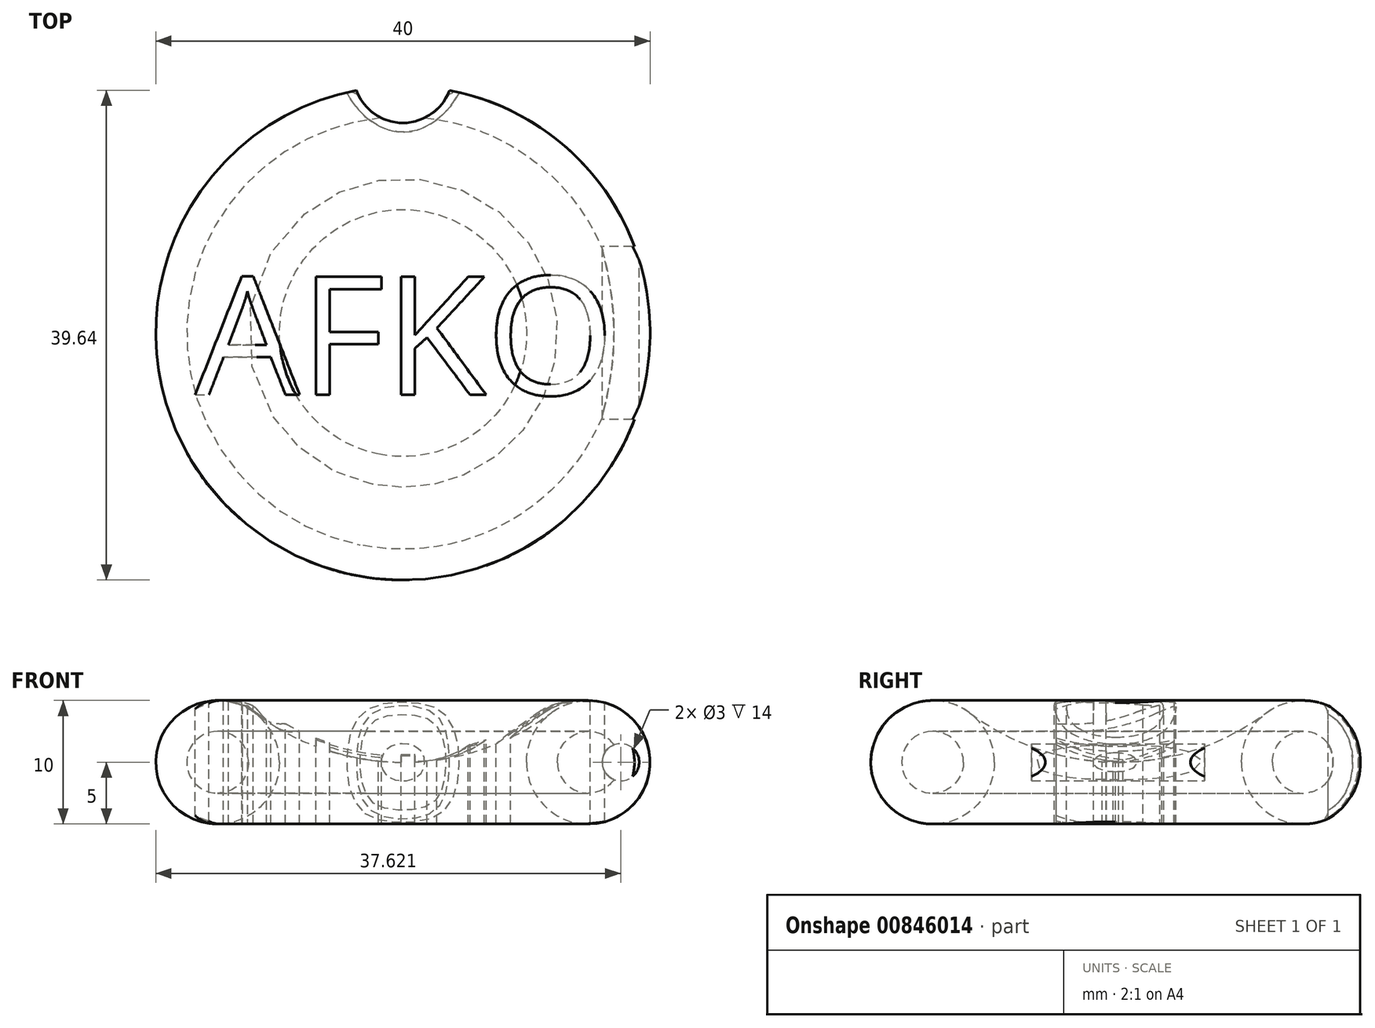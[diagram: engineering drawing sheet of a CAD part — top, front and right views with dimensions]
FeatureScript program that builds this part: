
annotation { "Feature Type Name" : "Feature", "Feature Type Description" : "" }
export const myFeature = defineFeature(function(context is Context, id is Id, definition is map)
    precondition{}
    {
        {
            var Q0;
            Q0=qCreatedBy(makeId("Front.planeOp"),FACE);
            var sketch = newSketch(context, id + "F0", { "sketchPlane" : qUnion([Q0])});
            skArc(sketch, "E0", {"start": v(-12, 9) * mm, "mid": v(-6.32, 6.03) * mm, "end": v(0, 5) * mm});
            skArc(sketch, "E1", {"start": v(-12, 9) * mm, "mid": v(-19.74, 6.58) * mm, "end": v(-15, 0) * mm});
            skLineSegment(sketch, "E2", {"start": v(-15, 0) * mm, "end": v(0, 0) * mm});
            skLineSegment(sketch, "E3", {"start": v(0, 0) * mm, "end": v(0, 5) * mm});
            skSolve(sketch);
        }
        {
            var Q0;
            Q0=makeQuery(id+"F0.imprint","IMPRINT",FACE,{"disambiguationData":[TD([[makeQuery(id+"F0.imprint","IMPRINT",EDGE,{"derivedFrom":sQuery(id+"F0.wireOp",EDGE,"E0")}),-1.0]])]});
            var Q1;
            Q1=sQuery(id+"F0.wireOp",EDGE,"E3");
            revolve(context, id + "F1", {"surfaceOperationType" : NewSurfaceOperationType.NEW, "entities" : qUnion([Q0]), "axis" : qUnion([Q1]), "revolveType" : RevolveType.FULL});
        }
        {
            var Q0;
            Q0=qCreatedBy(makeId("Top.planeOp"),FACE);
            cPlane(context, id + "F2", {"entities" : qUnion([Q0]), "cplaneType" : CPlaneType.OFFSET, "offset" : 25 * mm, "width" : 150 * mm, "height" : 150 * mm});
        }
        {
            var Q0;
            Q0=qCreatedBy(id+"F2.planeOp",FACE);
            var sketch = newSketch(context, id + "F3", { "sketchPlane" : qUnion([Q0])});
            skText(sketch, "E4", { "text": "AFKO", "fontName": "OpenSans-Regular.ttf"});
            const initialGuessF3  = {"E4": [-0.01682, -0.005, 1, 0, 0.00962]};
            skSetInitialGuess(sketch, initialGuessF3);
            skSolve(sketch);
        }
        {
            var Q0;
            Q0 = qSketchRegion(id + "F3", true);
            extrude(context, id + "F4", {"entities" : qUnion([Q0]), "operationType" : NewBodyOperationType.REMOVE, "oppositeDirection" : true, "depth" : 25 * mm, "offsetDistance" : 25 * mm});
        }
        {
            var Q0;
            Q0=qCreatedBy(makeId("Front.planeOp"),FACE);
            var sketch = newSketch(context, id + "F5", { "sketchPlane" : qUnion([Q0])});
            skCircle(sketch, "E5", {"center": v(-15, 5) * mm, "radius": 2.5 * mm});
            skCircle(sketch, "E6", {"center": v(-15, 5) * mm, "radius": 5 * mm});
            skSolve(sketch);
        }
        {
            var Q0;
            Q0 = qSketchRegion(id + "F5", true);
            var Q1;
            Q1=sQuery(id+"F0.wireOp",EDGE,"E3");
            revolve(context, id + "F6", {"surfaceOperationType" : NewSurfaceOperationType.NEW, "entities" : qUnion([Q0]), "axis" : qUnion([Q1]), "revolveType" : RevolveType.FULL});
        }
        {
            var Q0;
            Q0=qCreatedBy(id+"F2.planeOp",FACE);
            var sketch = newSketch(context, id + "F7", { "sketchPlane" : qUnion([Q0])});
            skCircle(sketch, "E7", {"center": v(0, 21) * mm, "radius": 4 * mm});
            skSolve(sketch);
        }
        {
            var Q0;
            Q0 = qSketchRegion(id + "F7", true);
            extrude(context, id + "F8", {"entities" : qUnion([Q0]), "operationType" : NewBodyOperationType.REMOVE, "endBound" : BoundingType.THROUGH_ALL, "oppositeDirection" : true, "depth" : 25 * mm, "offsetDistance" : 25 * mm});
        }
        {
            var Q0;
            Q0=makeQuery(id+"F8.boolean.opBoolean","INTERSECT",EDGE,{"derivedFrom":[makeQuery(id+"F6.opRevolve","SWEPT_FACE",FACE,{"disambiguationData":[OSD([sQuery(id+"F5.wireOp",EDGE,"E6")])]}),makeQuery(id+"F8.opExtrude","SWEPT_FACE",FACE,{"disambiguationData":[OSD([sQuery(id+"F7.wireOp",EDGE,"E7")])]})]});
            fillet(context, id + "F9", {"entities" : qUnion([Q0]), "radius" : 1 * mm, "tangentPropagation" : true, "allowEdgeOverflow" : false});
        }
        {
            var Q0;
            Q0=qCreatedBy(makeId("Front.planeOp"),FACE);
            var sketch = newSketch(context, id + "F10", { "sketchPlane" : qUnion([Q0])});
            skCircle(sketch, "E8", {"center": v(17.62, 5) * mm, "radius": 1.5 * mm});
            skSolve(sketch);
        }
        {
            var Q0;
            Q0 = qSketchRegion(id + "F10", true);
            extrude(context, id + "F11", {"entities" : qUnion([Q0]), "operationType" : NewBodyOperationType.REMOVE, "depth" : 7 * mm, "offsetDistance" : 25 * mm, "hasSecondDirection" : true, "secondDirectionOppositeDirection" : true, "secondDirectionDepth" : 7 * mm});
        }
    });
